# Revit family: Switch-Lutron-RadioRA_3_Outdoor_Plug-in_Switch_RR-15OUT-BL
name_source: partatom
category: Lighting Devices
units: mm (PartAtom-declared; Revit-internal decimal feet)

## family parameters
Cut with Voids When Loaded = No
Host = Face
Maintain Annotation Orientation = No
OmniClass Number = 23.85.80.11.27
OmniClass Title = Lighting Controls
Part Type = Normal
Room Calculation Point = No
Round Connector Dimension = Use Diameter
Shared = No

## types (1)
- RR-15OUT-BL
    Assembly Code = D5090900
    Cost = 0 $
    Default Elevation = 0"
    Description = Outdoor Plug-in Switch
    Finish = Plastic - Lutron - Black
    Instruction Sheet Link = https://webapiaw1proddat01st01.blob.core.windows.net
    Keynote = 26 27 00
    Manufacturer = Lutron Electronics Co., Inc
    Manufacturer Fax Number = 610-282-1243
    Maximum Operating Temperature = 122 °F
    Minimum Operating Temperature = -4 °F
    Model = RR-15OUT-BL
    Operating Voltage = 120 V
    Overall Depth = 2 5/16"
    Overall Height = 1 1/2"
    Overall Width = 19 1/4"
    Performance URL = https://www.lutron.com
    Product Documentation Link = https://www.lutron.com
    Product Name = RadioRA 3 Outdoor Plug-in Switch
    Product Page URL = https://radiora3.lutron.com
    Series = RadioRA 3
    URL = http://www.lutron.com
    Version = 2020 - v1.0a
    Video Link = https://www.youtube.com
    Voltage = 120 V
    Warranty URL = http://www.lutron.com

## geometry (parser evidence)
native form markers: Sweep x4
no freeform markers — native parametric forms only
